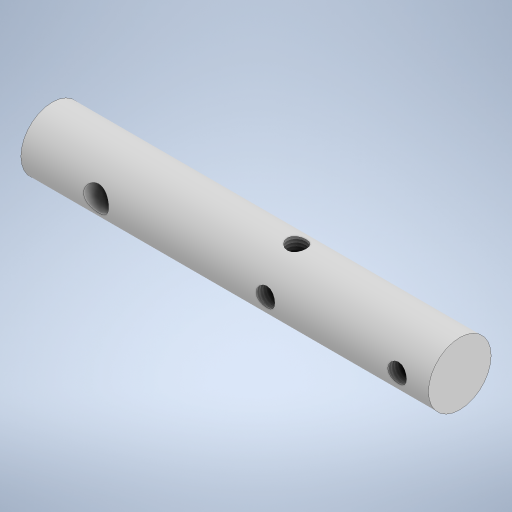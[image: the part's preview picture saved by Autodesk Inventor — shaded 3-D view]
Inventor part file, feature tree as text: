
AUTODESK INVENTOR PART (.ipt)
format: ipt  version: 2023 (Build 270158000, 158)  size: 280,064 bytes
history: native  units: mm
features: sketch x5, extrude x4, thread x3, other x1, hole x1
ambient origin geometry x8: Origin, YZ Plane, XZ Plane, XY Plane, X Axis, Y Axis, Z Axis, Center Point
bodies: Body1 (feature_tree)
feature tree (14):
  other  "Твердое тело1"
  extrude  "Выдавливание1"  Depth=10.0mm
  extrude  "Выдавливание2"  Depth=65.0mm TaperAngle=0.0deg
  extrude  "Выдавливание3"  Depth=12.0mm
  thread  "Резьба1"
  thread  "Резьба2"
  extrude  "Выдавливание4"  Depth=4.0mm
  thread  "Резьба3"
  hole  "Отверстие1"  [1 undecoded]
  sketch  "Эскиз1"
  sketch  "Эскиз2"
  sketch  "Эскиз3"
  sketch  "Эскиз4"
  sketch  "Эскиз5"
note: 1 required parameter value undecoded (feature->parameter linkage not recoverable at this tier; creation-order binding heuristic only, values carry confidence <= 0.55)
